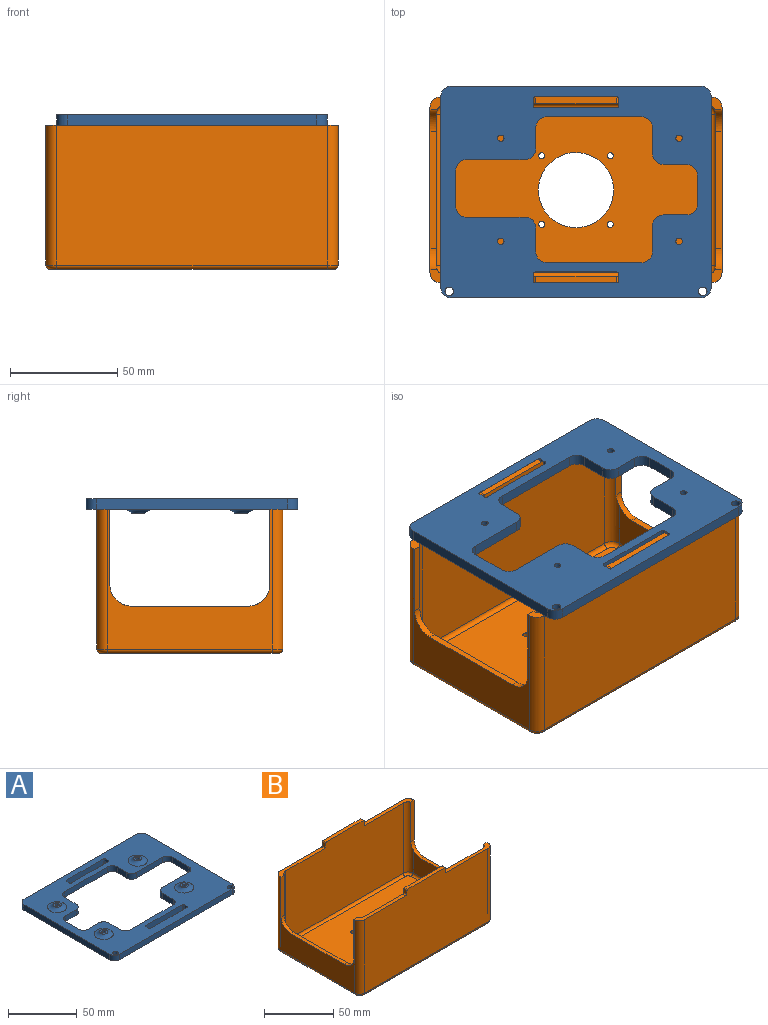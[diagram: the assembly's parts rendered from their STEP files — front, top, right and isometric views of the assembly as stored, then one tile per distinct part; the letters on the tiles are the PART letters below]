
ASSEMBLY  parts=2 mates=1
PART A: 64 faces, bbox 126x98.5x10 mm
  f0: plane 126x98.5mm, normal (0,0,1), area 6190.5mm2, adj f2,f3,f4,f5,f6,f7,f8,f9
  f1: plane 126x98.5mm, normal (0,0,-1), area 6778mm2, adj f2,f3,f4,f5,f6,f7,f8,f9
  f2: plane 5x3mm, normal (-1,0,0), area 15mm2, adj f0,f1,f22,f25
  f3: plane 38x5mm, normal (0,1,0), area 190mm2, adj f0,f1,f22,f23
  f4: plane 5x3mm, normal (1,0,0), area 15mm2, adj f0,f1,f23,f24
  f5: plane 116x5mm, normal (0,1,0), area 580mm2, adj f0,f1,f28,f29
  f6: plane 88.5x5mm, normal (-1,0,0), area 442.5mm2, adj f0,f1,f28,f30
  f7: plane 116x5mm, normal (0,-1,0), area 580mm2, adj f0,f1,f30,f31
  f8: plane 5x3mm, normal (1,0,0), area 15mm2, adj f0,f1,f20,f27
  f9: plane 38x5mm, normal (0,-1,0), area 190mm2, adj f0,f1,f20,f21
  f10: plane 5x3mm, normal (-1,0,0), area 15mm2, adj f0,f1,f21,f26
  f11: cylinder r=1.5mm len=7mm, axis (0,0,-1), area 66mm2, adj f1,f33
  f12: cylinder r=1.5mm len=7mm, axis (0,0,-1), area 66mm2, adj f1,f34
  f13: cylinder r=1.5mm len=7mm, axis (0,0,-1), area 66mm2, adj f1,f35
  f14: plane 38x5mm, normal (0,-1,0), area 190mm2, adj f0,f1,f24,f25
  f15: cylinder r=2mm len=5mm, axis (0,0,-1), area 62.8mm2, adj f0,f1
  f16: cylinder r=2mm len=5mm, axis (0,0,-1), area 62.8mm2, adj f0,f1
  f17: plane 88.5x5mm, normal (1,0,0), area 442.5mm2, adj f0,f1,f29,f31
  f18: plane 38x5mm, normal (0,1,0), area 190mm2, adj f0,f1,f26,f27
  f19: cylinder r=1.5mm len=7mm, axis (0,0,-1), area 66mm2, adj f1,f32
  f20: cylinder r=1mm len=5mm, axis (0,0,-1), area 7.9mm2, adj f0,f1,f8,f9
  f21: cylinder r=1mm len=5mm, axis (0,0,1), area 7.9mm2, adj f0,f1,f9,f10
  f22: cylinder r=1mm len=5mm, axis (0,0,1), area 7.9mm2, adj f0,f1,f2,f3
  f23: cylinder r=1mm len=5mm, axis (0,0,-1), area 7.9mm2, adj f0,f1,f3,f4
  f24: cylinder r=1mm len=5mm, axis (0,0,1), area 7.9mm2, adj f0,f1,f4,f14
  f25: cylinder r=1mm len=5mm, axis (0,0,-1), area 7.9mm2, adj f0,f1,f2,f14
  f26: cylinder r=1mm len=5mm, axis (0,0,-1), area 7.9mm2, adj f0,f1,f10,f18
  f27: cylinder r=1mm len=5mm, axis (0,0,1), area 7.9mm2, adj f0,f1,f8,f18
  f28: cylinder r=5mm len=5mm, axis (0,0,1), area 39.3mm2, adj f0,f1,f5,f6
  f29: cylinder r=5mm len=5mm, axis (0,0,-1), area 39.3mm2, adj f0,f1,f5,f17
  f30: cylinder r=5mm len=5mm, axis (0,0,-1), area 39.3mm2, adj f0,f1,f6,f7
  f31: cylinder r=5mm len=5mm, axis (0,0,1), area 39.3mm2, adj f0,f1,f7,f17
  f32: plane 6x6mm, normal (0,0,1), area 21.2mm2, adj f19,f39
  f33: plane 6x6mm, normal (0,0,1), area 21.2mm2, adj f11,f38
  f34: plane 6x6mm, normal (0,0,1), area 21.2mm2, adj f12,f37
  f35: plane 6x6mm, normal (0,0,1), area 21.2mm2, adj f13,f36
  f36: torus R=7mm, axis (0,0,1), area 141.1mm2, adj f0,f35
  f37: torus R=7mm, axis (0,0,1), area 141.1mm2, adj f0,f34
  f38: torus R=7mm, axis (0,0,1), area 141.1mm2, adj f0,f33
  f39: torus R=7mm, axis (0,0,1), area 141.1mm2, adj f0,f32
  f40: plane 10.92x5mm, normal (0,-1,0), area 54.6mm2, adj f0,f1,f52,f55
  f41: plane 13.53x5mm, normal (1,0,0), area 67.7mm2, adj f0,f1,f52,f53
  f42: plane 10.92x5mm, normal (0,1,0), area 54.6mm2, adj f0,f1,f53,f54
  f43: plane 12.23x5mm, normal (1,0,0), area 61.2mm2, adj f0,f1,f54,f61
  f44: plane 44.32x5mm, normal (0,1,0), area 221.6mm2, adj f0,f1,f61,f62
  f45: plane 11.15x5mm, normal (-1,0,0), area 55.7mm2, adj f0,f1,f57,f62
  f46: plane 27.23x5mm, normal (0,1,0), area 136.2mm2, adj f0,f1,f57,f58
  f47: plane 16.9x5mm, normal (-1,0,0), area 84.5mm2, adj f0,f1,f58,f59
  f48: plane 27.23x5mm, normal (0,-1,0), area 136.2mm2, adj f0,f1,f56,f59
  f49: plane 9.84x5mm, normal (-1,0,0), area 49.2mm2, adj f0,f1,f56,f63
  f50: plane 44.32x5mm, normal (0,-1,0), area 221.6mm2, adj f0,f1,f60,f63
  f51: plane 12.12x5mm, normal (1,0,0), area 60.6mm2, adj f0,f1,f55,f60
  f52: cylinder r=5mm len=5mm, axis (0,0,1), area 39.3mm2, adj f0,f1,f40,f41
  f53: cylinder r=5mm len=5mm, axis (0,0,-1), area 39.3mm2, adj f0,f1,f41,f42
  f54: cylinder r=5mm len=5mm, axis (0,0,1), area 39.3mm2, adj f0,f1,f42,f43
  f55: cylinder r=5mm len=5mm, axis (0,0,-1), area 39.3mm2, adj f0,f1,f40,f51
  f56: cylinder r=5mm len=5mm, axis (0,0,1), area 39.3mm2, adj f0,f1,f48,f49
  f57: cylinder r=5mm len=5mm, axis (0,0,-1), area 39.3mm2, adj f0,f1,f45,f46
  f58: cylinder r=5mm len=5mm, axis (0,0,1), area 39.3mm2, adj f0,f1,f46,f47
  f59: cylinder r=5mm len=5mm, axis (0,0,-1), area 39.3mm2, adj f0,f1,f47,f48
  f60: cylinder r=5mm len=5mm, axis (0,0,1), area 39.3mm2, adj f0,f1,f50,f51
  f61: cylinder r=5mm len=5mm, axis (0,0,-1), area 39.3mm2, adj f0,f1,f43,f44
  f62: cylinder r=5mm len=5mm, axis (0,0,1), area 39.3mm2, adj f0,f1,f44,f45
  f63: cylinder r=5mm len=5mm, axis (0,0,-1), area 39.3mm2, adj f0,f1,f49,f50
PART B: 67 faces, bbox 136.8x87.3x72 mm
  f0: plane 47.15x6mm, normal (0,0,1), area 150.2mm2, adj f2,f14,f17,f28,f36,f43,f44
  f1: plane 47.15x6mm, normal (0,0,1), area 150.2mm2, adj f12,f15,f16,f19,f40,f47,f48
  f2: plane 76.5x65mm, normal (-1,0,0), area 1660.7mm2, adj f0,f3,f24,f25,f26,f27,f28,f44
  f3: plane 47.15x6mm, normal (0,0,1), area 150.2mm2, adj f2,f12,f15,f27,f39,f49,f50
  f4: cylinder r=1.4mm len=3mm, axis (0,0,-1), area 26.4mm2, adj f9,f10
  f5: cylinder r=1.4mm len=3mm, axis (0,0,-1), area 26.4mm2, adj f9,f10
  f6: cylinder r=1.4mm len=3mm, axis (0,0,-1), area 26.4mm2, adj f9,f10
  f7: cylinder r=1.4mm len=3mm, axis (0,0,-1), area 26.4mm2, adj f9,f10
  f8: cylinder r=17.5mm len=35mm, axis (0,0,-1), area 329.9mm2, adj f9,f10
  f9: plane 126x76.5mm, normal (0,0,1), area 8644.5mm2, adj f4,f5,f6,f7,f8,f59,f60,f61
  f10: plane 132x82.5mm, normal (0,0,-1), area 9895.5mm2, adj f4,f5,f6,f7,f8,f51,f52,f53
  f11: plane 70.5x20.97mm, normal (1,0,0), area 1215.7mm2, adj f24,f25,f26,f43,f49,f62
  f12: plane 120x67mm, normal (0,1,0), area 7638.5mm2, adj f1,f3,f29,f30,f31,f39,f40,f41
  f13: plane 70.5x20.97mm, normal (-1,0,0), area 1215.7mm2, adj f20,f21,f23,f45,f48,f63
  f14: plane 120x67mm, normal (0,-1,0), area 7638.5mm2, adj f0,f18,f32,f33,f34,f35,f36,f37
  f15: plane 126x70mm, normal (0,-1,0), area 8388.5mm2, adj f1,f3,f29,f30,f31,f39,f40,f41
  f16: plane 76.5x65mm, normal (1,0,0), area 1660.7mm2, adj f1,f18,f19,f20,f21,f22,f23,f46
  f17: plane 126x70mm, normal (0,1,0), area 8388.5mm2, adj f0,f18,f32,f33,f34,f35,f36,f37
  f18: plane 47.15x6mm, normal (0,0,1), area 150.2mm2, adj f14,f16,f17,f22,f35,f45,f46
  f19: plane 35.03x3.42mm, normal (0,1,0), area 119.7mm2, adj f1,f16,f23,f48
  f20: plane 54.5x3mm, normal (0,0,1), area 163.5mm2, adj f13,f16,f21,f23
  f21: cylinder r=10mm len=10mm, axis (-1,0,0), area 48.5mm2, adj f13,f16,f20,f22,f45
  f22: plane 35.03x3.42mm, normal (0,-1,0), area 119.7mm2, adj f16,f18,f21,f45
  f23: cylinder r=10mm len=10mm, axis (-1,0,0), area 48.5mm2, adj f13,f16,f19,f20,f48
  f24: cylinder r=10mm len=10mm, axis (-1,0,0), area 48.5mm2, adj f2,f11,f26,f27,f49
  f25: cylinder r=10mm len=10mm, axis (-1,0,0), area 48.5mm2, adj f2,f11,f26,f28,f43
  f26: plane 54.5x3mm, normal (0,0,1), area 163.5mm2, adj f2,f11,f24,f25
  f27: plane 35.03x3.42mm, normal (0,1,0), area 119.7mm2, adj f2,f3,f24,f49
  f28: plane 35.03x3.42mm, normal (0,-1,0), area 119.7mm2, adj f0,f2,f25,f43
  f29: plane 3x3mm, normal (1,0,0), area 9mm2, adj f12,f15,f40,f42
  f30: plane 3x3mm, normal (-1,0,0), area 9mm2, adj f12,f15,f39,f41
  f31: plane 37.7x3mm, normal (0,0,1), area 113.1mm2, adj f12,f15,f41,f42
  f32: plane 3x3mm, normal (-1,0,0), area 9mm2, adj f14,f17,f36,f38
  f33: plane 3x3mm, normal (1,0,0), area 9mm2, adj f14,f17,f35,f37
  f34: plane 37.7x3mm, normal (0,0,1), area 113.1mm2, adj f14,f17,f37,f38
  f35: cylinder r=1mm len=3mm, axis (0,1,0), area 4.7mm2, adj f14,f17,f18,f33
  f36: cylinder r=1mm len=3mm, axis (0,-1,0), area 4.7mm2, adj f0,f14,f17,f32
  f37: cylinder r=1mm len=3mm, axis (0,-1,0), area 4.7mm2, adj f14,f17,f33,f34
  f38: cylinder r=1mm len=3mm, axis (0,1,0), area 4.7mm2, adj f14,f17,f32,f34
  f39: cylinder r=1mm len=3mm, axis (0,-1,0), area 4.7mm2, adj f3,f12,f15,f30
  f40: cylinder r=1mm len=3mm, axis (0,1,0), area 4.7mm2, adj f1,f12,f15,f29
  f41: cylinder r=1mm len=3mm, axis (0,1,0), area 4.7mm2, adj f12,f15,f30,f31
  f42: cylinder r=1mm len=3mm, axis (0,-1,0), area 4.7mm2, adj f12,f15,f29,f31
  f43: cylinder r=5mm len=62mm, axis (0,0,1), area 406.5mm2, adj f0,f11,f14,f25,f28,f60
  f44: cylinder r=5mm len=65mm, axis (0,0,-1), area 510.5mm2, adj f0,f2,f17,f56
  f45: cylinder r=5mm len=62mm, axis (0,0,-1), area 406.5mm2, adj f13,f14,f18,f21,f22,f61
  f46: cylinder r=5mm len=65mm, axis (0,0,1), area 510.5mm2, adj f16,f17,f18,f57
  f47: cylinder r=5mm len=65mm, axis (0,0,-1), area 510.5mm2, adj f1,f15,f16,f53
  f48: cylinder r=5mm len=62mm, axis (0,0,1), area 406.5mm2, adj f1,f12,f13,f19,f23,f65
  f49: cylinder r=5mm len=62mm, axis (0,0,-1), area 406.5mm2, adj f3,f11,f12,f24,f27,f64
  f50: cylinder r=5mm len=65mm, axis (0,0,1), area 510.5mm2, adj f2,f3,f15,f52
  f51: cylinder r=2mm len=126mm, axis (1,0,0), area 395.8mm2, adj f10,f15,f52,f53
  f52: torus R=3mm, axis (0,0,1), area 21.1mm2, adj f10,f50,f51,f54
  f53: torus R=3mm, axis (0,0,1), area 21.1mm2, adj f10,f47,f51,f55
  f54: cylinder r=2mm len=76.5mm, axis (0,-1,0), area 240.3mm2, adj f2,f10,f52,f56
  f55: cylinder r=2mm len=76.5mm, axis (0,1,0), area 240.3mm2, adj f10,f16,f53,f57
  f56: torus R=3mm, axis (0,0,1), area 21.1mm2, adj f10,f44,f54,f58
  f57: torus R=3mm, axis (0,0,1), area 21.1mm2, adj f10,f46,f55,f58
  f58: cylinder r=2mm len=126mm, axis (-1,0,0), area 395.8mm2, adj f10,f17,f56,f57
  f59: cylinder r=2mm len=120mm, axis (1,0,0), area 377mm2, adj f9,f14,f60,f61
  f60: torus R=3mm, axis (0,0,1), area 21.1mm2, adj f9,f43,f59,f62
  f61: torus R=3mm, axis (0,0,1), area 21.1mm2, adj f9,f45,f59,f63
  f62: cylinder r=2mm len=70.5mm, axis (0,1,0), area 221.5mm2, adj f9,f11,f60,f64
  f63: cylinder r=2mm len=70.5mm, axis (0,-1,0), area 221.5mm2, adj f9,f13,f61,f65
  f64: torus R=3mm, axis (0,0,1), area 21.1mm2, adj f9,f49,f62,f66
  f65: torus R=3mm, axis (0,0,1), area 21.1mm2, adj f9,f48,f63,f66
  f66: cylinder r=2mm len=120mm, axis (-1,0,0), area 377mm2, adj f9,f12,f64,f65
PLACE A rot(axis=(0,1,0),180deg) t=(97.63,40.8,107.17)mm
PLACE B t=(79.76,43.8,35.17)mm
MATE fastened A.f1 <-> B.f31  axis (0,0,1) through (84.39,47.8,107.17)mm
